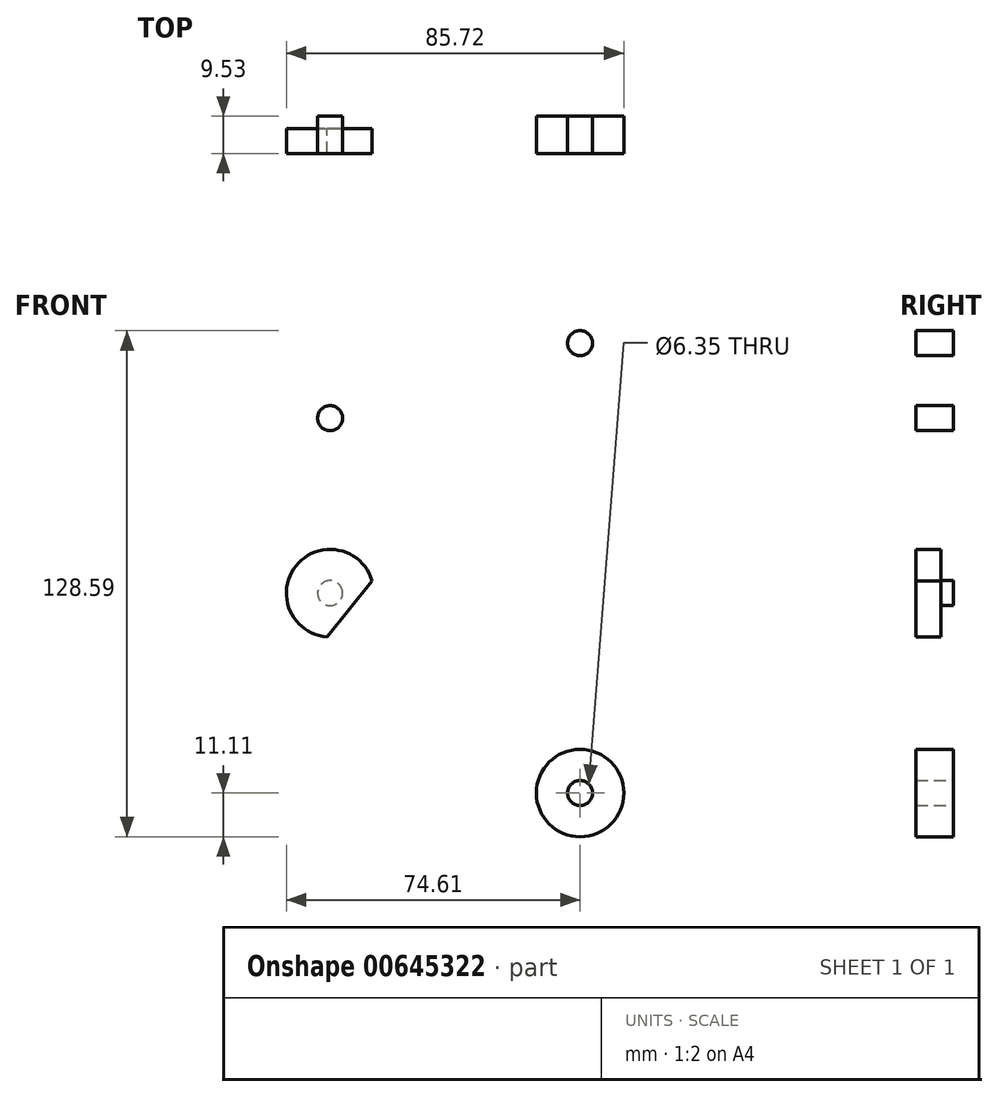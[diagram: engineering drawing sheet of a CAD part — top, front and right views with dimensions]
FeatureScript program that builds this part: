
annotation { "Feature Type Name" : "Feature", "Feature Type Description" : "" }
export const myFeature = defineFeature(function(context is Context, id is Id, definition is map)
    precondition{}
    {
        {
            var Q0;
            Q0=qCreatedBy(makeId("Front.planeOp"),FACE);
            var sketch = newSketch(context, id + "F0", { "sketchPlane" : qUnion([Q0])});
            skLineSegment(sketch, "E0", {"start": v(0, 0) * mm, "end": v(0, 63.5) * mm, "construction": true});
            skLineSegment(sketch, "E1", {"start": v(0, 0) * mm, "end": v(0, -50.8) * mm, "construction": true});
            skCircle(sketch, "E2", {"center": v(0, 0) * mm, "radius": 3.98 * mm});
            skCircle(sketch, "E3", {"center": v(0, 0) * mm, "radius": 15.88 * mm});
            skCircle(sketch, "E4", {"center": v(0, 63.5) * mm, "radius": 3.18 * mm});
            skCircle(sketch, "E5", {"center": v(0, -50.8) * mm, "radius": 3.18 * mm});
            skLineSegment(sketch, "E6", {"start": v(0, 63.5) * mm, "end": v(-44.45, 63.5) * mm, "construction": true});
            skCircle(sketch, "E7", {"center": v(0, 63.5) * mm, "radius": 11.11 * mm});
            skCircle(sketch, "E8", {"center": v(0, -50.8) * mm, "radius": 11.11 * mm});
            skCircle(sketch, "E9", {"center": v(-44.45, 63.5) * mm, "radius": 3.18 * mm});
            skCircle(sketch, "E10", {"center": v(-44.45, 63.5) * mm, "radius": 7.94 * mm});
            skLineSegment(sketch, "E11", {"start": v(0, 0) * mm, "end": v(-63.5, 0) * mm, "construction": true});
            skCircle(sketch, "E12", {"center": v(-63.5, 0) * mm, "radius": 3.18 * mm});
            skCircle(sketch, "E13", {"center": v(-63.5, 0) * mm, "radius": 11.11 * mm});
            skLineSegment(sketch, "E14", {"start": v(-63.5, 0) * mm, "end": v(-63.5, 44.45) * mm, "construction": true});
            skCircle(sketch, "E15", {"center": v(-63.5, 44.45) * mm, "radius": 3.18 * mm});
            skCircle(sketch, "E16", {"center": v(-63.5, 44.45) * mm, "radius": 7.94 * mm});
            skCircle(sketch, "E17", {"center": v(-42.85, 0) * mm, "radius": 3.18 * mm});
            skLineSegment(sketch, "E18", {"start": v(-0.8, 74.58) * mm, "end": v(-45.02, 71.42) * mm});
            skLineSegment(sketch, "E19", {"start": v(11.08, 64.33) * mm, "end": v(15.83, 1.2) * mm});
            skLineSegment(sketch, "E20", {"start": v(11.06, -51.84) * mm, "end": v(15.8, -1.49) * mm});
            skCircle(sketch, "E21", {"center": v(3.18, -36.39) * mm, "radius": 3.18 * mm});
            skLineSegment(sketch, "E22", {"start": v(3.18, -36.39) * mm, "end": v(0, -36.39) * mm, "construction": true});
            skLineSegment(sketch, "E23", {"start": v(-11.06, -51.84) * mm, "end": v(-15.95, 0) * mm});
            skLineSegment(sketch, "E24", {"start": v(-1.2, -15.83) * mm, "end": v(-64.33, -11.08) * mm});
            skLineSegment(sketch, "E25", {"start": v(-74.58, 0.8) * mm, "end": v(-71.42, 45.02) * mm});
            skLineSegment(sketch, "E26", {"start": v(-45.02, 55.58) * mm, "end": v(-19.88, 53.78) * mm});
            skLineSegment(sketch, "E27", {"start": v(-15.83, 1.2) * mm, "end": v(-12.52, 45.26) * mm});
            skArc(sketch, "E28.filletArc", {"start": v(-12.52, 45.26) * mm, "mid": v(-14.43, 51.05) * mm, "end": v(-19.88, 53.78) * mm});
            skLineSegment(sketch, "E29", {"start": v(-45.26, 12.52) * mm, "end": v(-1.2, 15.83) * mm});
            skLineSegment(sketch, "E30", {"start": v(-53.78, 19.88) * mm, "end": v(-55.58, 45.02) * mm});
            skArc(sketch, "E31.filletArc", {"start": v(-53.78, 19.88) * mm, "mid": v(-51.05, 14.43) * mm, "end": v(-45.26, 12.52) * mm});
            skCircle(sketch, "E32", {"center": v(0, 0) * mm, "radius": 3.18 * mm});
            skSolve(sketch);
        }
        {
            var Q0;
            {var subQ0=sQuery(id+"F0.wireOp",EDGE,"E18");Q0=makeQuery(id+"F0.imprint","IMPRINT",FACE,{"disambiguationData":[TD([[makeQuery(id+"F0.imprint","IMPRINT",EDGE,{"derivedFrom":subQ0}),1.0]])]});}
            var Q1;
            Q1=makeQuery(id+"F0.imprint","IMPRINT",FACE,{"disambiguationData":[TD([[makeQuery(id+"F0.imprint","IMPRINT",EDGE,{"derivedFrom":sQuery(id+"F0.wireOp",EDGE,"E9")}),-1.0]])]});
            var Q2;
            Q2=makeQuery(id+"F0.imprint","IMPRINT",FACE,{"disambiguationData":[TD([[makeQuery(id+"F0.imprint","IMPRINT",EDGE,{"derivedFrom":sQuery(id+"F0.wireOp",EDGE,"E4")}),-1.0]])]});
            var Q3;
            {var subQ0=sQuery(id+"F0.wireOp",EDGE,"E27");var subQ1=sQuery(id+"F0.wireOp",EDGE,"E3");var subQ2=makeQuery(id+"F0.imprint","INTERSECT",VERTEX,{"derivedFrom":[subQ1,subQ0]});Q3=makeQuery(id+"F0.imprint","IMPRINT",FACE,{"disambiguationData":[TD([[makeQuery(id+"F0.imprint","IMPRINT",EDGE,{"disambiguationData":[TD([[subQ2,1.0]])],"derivedFrom":subQ1}),-1.0]])]});}
            var Q4;
            Q4=makeQuery(id+"F0.imprint","IMPRINT",FACE,{"disambiguationData":[TD([[makeQuery(id+"F0.imprint","IMPRINT",EDGE,{"derivedFrom":sQuery(id+"F0.wireOp",EDGE,"E2")}),-1.0]])]});
            var Q5;
            {var subQ0=sQuery(id+"F0.wireOp",EDGE,"E20");Q5=makeQuery(id+"F0.imprint","IMPRINT",FACE,{"disambiguationData":[TD([[makeQuery(id+"F0.imprint","IMPRINT",EDGE,{"derivedFrom":subQ0}),1.0]])]});}
            var Q6;
            {var subQ0=sQuery(id+"F0.wireOp",EDGE,"E24");var subQ1=sQuery(id+"F0.wireOp",EDGE,"E3");var subQ2=makeQuery(id+"F0.imprint","INTERSECT",VERTEX,{"derivedFrom":[subQ1,subQ0]});Q6=makeQuery(id+"F0.imprint","IMPRINT",FACE,{"disambiguationData":[TD([[makeQuery(id+"F0.imprint","IMPRINT",EDGE,{"disambiguationData":[TD([[subQ2,1.0]])],"derivedFrom":subQ1}),-1.0]])]});}
            var Q7;
            Q7=makeQuery(id+"F0.imprint","IMPRINT",FACE,{"disambiguationData":[TD([[makeQuery(id+"F0.imprint","IMPRINT",EDGE,{"derivedFrom":sQuery(id+"F0.wireOp",EDGE,"E5")}),-1.0]])]});
            var Q8;
            Q8=makeQuery(id+"F0.imprint","IMPRINT",FACE,{"disambiguationData":[TD([[makeQuery(id+"F0.imprint","IMPRINT",EDGE,{"derivedFrom":sQuery(id+"F0.wireOp",EDGE,"E2")}),1.0]])]});
            extrude(context, id + "F1", {"entities" : qUnion([Q0, Q1, Q2, Q3, Q4, Q5, Q6, Q7, Q8]), "oppositeDirection" : true, "depth" : 3.17 * mm, "offsetDistance" : 25.4 * mm});
        }
        {
            var Q0;
            Q0=makeQuery(id+"F0.imprint","IMPRINT",FACE,{"disambiguationData":[TD([[makeQuery(id+"F0.imprint","IMPRINT",EDGE,{"derivedFrom":sQuery(id+"F0.wireOp",EDGE,"E17")}),-1.0]])]});
            var Q1;
            Q1=makeQuery(id+"F0.imprint","IMPRINT",FACE,{"disambiguationData":[TD([[makeQuery(id+"F0.imprint","IMPRINT",EDGE,{"derivedFrom":sQuery(id+"F0.wireOp",EDGE,"E15")}),-1.0]])]});
            var Q2;
            Q2=makeQuery(id+"F0.imprint","IMPRINT",FACE,{"disambiguationData":[TD([[makeQuery(id+"F0.imprint","IMPRINT",EDGE,{"derivedFrom":sQuery(id+"F0.wireOp",EDGE,"E12")}),-1.0]])]});
            var Q3;
            {var subQ0=sQuery(id+"F0.wireOp",EDGE,"E27");var subQ1=sQuery(id+"F0.wireOp",EDGE,"E3");var subQ2=makeQuery(id+"F0.imprint","INTERSECT",VERTEX,{"derivedFrom":[subQ1,subQ0]});Q3=makeQuery(id+"F0.imprint","IMPRINT",FACE,{"disambiguationData":[TD([[makeQuery(id+"F0.imprint","IMPRINT",EDGE,{"disambiguationData":[TD([[subQ2,1.0]])],"derivedFrom":subQ1}),-1.0]])]});}
            var Q4;
            Q4=makeQuery(id+"F0.imprint","IMPRINT",FACE,{"disambiguationData":[TD([[makeQuery(id+"F0.imprint","IMPRINT",EDGE,{"derivedFrom":sQuery(id+"F0.wireOp",EDGE,"E2")}),-1.0]])]});
            var Q5;
            {var subQ0=sQuery(id+"F0.wireOp",EDGE,"E24");var subQ1=sQuery(id+"F0.wireOp",EDGE,"E3");var subQ2=makeQuery(id+"F0.imprint","INTERSECT",VERTEX,{"derivedFrom":[subQ1,subQ0]});Q5=makeQuery(id+"F0.imprint","IMPRINT",FACE,{"disambiguationData":[TD([[makeQuery(id+"F0.imprint","IMPRINT",EDGE,{"disambiguationData":[TD([[subQ2,1.0]])],"derivedFrom":subQ1}),-1.0]])]});}
            var Q6;
            Q6=makeQuery(id+"F0.imprint","IMPRINT",FACE,{"disambiguationData":[TD([[makeQuery(id+"F0.imprint","IMPRINT",EDGE,{"derivedFrom":sQuery(id+"F0.wireOp",EDGE,"E2")}),1.0]])]});
            extrude(context, id + "F2", {"entities" : qUnion([Q0, Q1, Q2, Q3, Q4, Q5, Q6]), "depth" : 3.17 * mm, "offsetDistance" : 25.4 * mm});
        }
        {
            var Q0;
            Q0=makeQuery(id+"F1.opExtrude","CAP_FACE",FACE,{"disambiguationData":[OSD([sQuery(id+"F0.wireOp",EDGE,"E3"),sQuery(id+"F0.wireOp",EDGE,"E4"),sQuery(id+"F0.wireOp",EDGE,"E5"),sQuery(id+"F0.wireOp",EDGE,"E7"),sQuery(id+"F0.wireOp",EDGE,"E8"),sQuery(id+"F0.wireOp",EDGE,"E9"),sQuery(id+"F0.wireOp",EDGE,"E10"),sQuery(id+"F0.wireOp",EDGE,"E18"),sQuery(id+"F0.wireOp",EDGE,"E19"),sQuery(id+"F0.wireOp",EDGE,"E20"),sQuery(id+"F0.wireOp",EDGE,"E21"),sQuery(id+"F0.wireOp",EDGE,"E23"),sQuery(id+"F0.wireOp",EDGE,"E26"),sQuery(id+"F0.wireOp",EDGE,"E27"),sQuery(id+"F0.wireOp",EDGE,"E28.filletArc"),sQuery(id+"F0.wireOp",EDGE,"E32")])],"isStart":false});
            var sketch = newSketch(context, id + "F3", { "sketchPlane" : qUnion([Q0])});
            skCircle(sketch, "E33", {"center": v(0, 0) * mm, "radius": 3.98 * mm});
            skCircle(sketch, "E34", {"center": v(0, -50.8) * mm, "radius": 11.11 * mm});
            skSolve(sketch);
        }
        {
            var Q0;
            Q0=makeQuery(id+"F0.imprint","IMPRINT",FACE,{"disambiguationData":[TD([[makeQuery(id+"F0.imprint","IMPRINT",EDGE,{"derivedFrom":sQuery(id+"F0.wireOp",EDGE,"E12")}),-1.0]])]});
            var sketch = newSketch(context, id + "F4", { "sketchPlane" : qUnion([Q0])});
            skCircle(sketch, "E35", {"center": v(-63.5, 0) * mm, "radius": 11.11 * mm});
            skSolve(sketch);
        }
        {
            var Q0;
            Q0=qCreatedBy(makeId("Front.planeOp"),FACE);
            cPlane(context, id + "F5", {"entities" : qUnion([Q0]), "cplaneType" : CPlaneType.OFFSET, "offset" : 9.52 * mm, "width" : 152.4 * mm, "height" : 152.4 * mm});
        }
        {
            var Q0;
            Q0=makeQuery(id+"F0.imprint","IMPRINT",FACE,{"disambiguationData":[TD([[makeQuery(id+"F0.imprint","IMPRINT",EDGE,{"derivedFrom":sQuery(id+"F0.wireOp",EDGE,"E17")}),-1.0]])]});
            var sketch = newSketch(context, id + "F6", { "sketchPlane" : qUnion([Q0])});
            skLineSegment(sketch, "E36", {"start": v(-52.84, 3.15) * mm, "end": v(-64.24, -11.09) * mm});
            skLineSegment(sketch, "E37", {"start": v(0, -50.8) * mm, "end": v(-58.54, -3.97) * mm, "construction": true});
            skCircle(sketch, "E38.0", {"center": v(-63.5, 0) * mm, "radius": 11.11 * mm});
            skSolve(sketch);
        }
        {
            var Q0;
            {var subQ0=sQuery(id+"F6.wireOp",EDGE,"E36");Q0=makeQuery(id+"F6.imprint","IMPRINT",FACE,{"disambiguationData":[TD([[makeQuery(id+"F6.imprint","IMPRINT",EDGE,{"derivedFrom":subQ0}),-1.0]])]});}
            var Q1;
            Q1=makeQuery(id+"F0.imprint","IMPRINT",FACE,{"disambiguationData":[TD([[makeQuery(id+"F0.imprint","IMPRINT",EDGE,{"derivedFrom":sQuery(id+"F0.wireOp",EDGE,"E5")}),-1.0]])]});
            var Q2;
            Q2=makeQuery(id+"F0.imprint","IMPRINT",FACE,{"disambiguationData":[TD([[makeQuery(id+"F0.imprint","IMPRINT",EDGE,{"derivedFrom":sQuery(id+"F0.wireOp",EDGE,"E4")}),1.0]])]});
            var Q3;
            Q3=makeQuery(id+"F0.imprint","IMPRINT",FACE,{"disambiguationData":[TD([[makeQuery(id+"F0.imprint","IMPRINT",EDGE,{"derivedFrom":sQuery(id+"F0.wireOp",EDGE,"E15")}),1.0]])]});
            var Q4;
            Q4=qCreatedBy(id+"F5.planeOp",FACE);
            extrude(context, id + "F7", {"entities" : qUnion([Q0, Q1, Q2, Q3]), "endBound" : BoundingType.UP_TO_SURFACE, "depth" : 25.4 * mm, "endBoundEntityFace" : qUnion([Q4]), "offsetDistance" : 25.4 * mm});
        }
        {
            var Q0;
            Q0=makeQuery(id+"F2.opExtrude","SWEPT_BODY",BODY,{"disambiguationData":[OSD([sQuery(id+"F0.wireOp",EDGE,"E3"),sQuery(id+"F0.wireOp",EDGE,"E12"),sQuery(id+"F0.wireOp",EDGE,"E13"),sQuery(id+"F0.wireOp",EDGE,"E15"),sQuery(id+"F0.wireOp",EDGE,"E16"),sQuery(id+"F0.wireOp",EDGE,"E17"),sQuery(id+"F0.wireOp",EDGE,"E24"),sQuery(id+"F0.wireOp",EDGE,"E25"),sQuery(id+"F0.wireOp",EDGE,"E29"),sQuery(id+"F0.wireOp",EDGE,"E30"),sQuery(id+"F0.wireOp",EDGE,"E31.filletArc"),sQuery(id+"F0.wireOp",EDGE,"E32")])]});
            var Q1;
            Q1=makeQuery(id+"F1.opExtrude","SWEPT_BODY",BODY,{"disambiguationData":[OSD([sQuery(id+"F0.wireOp",EDGE,"E3"),sQuery(id+"F0.wireOp",EDGE,"E4"),sQuery(id+"F0.wireOp",EDGE,"E5"),sQuery(id+"F0.wireOp",EDGE,"E7"),sQuery(id+"F0.wireOp",EDGE,"E8"),sQuery(id+"F0.wireOp",EDGE,"E9"),sQuery(id+"F0.wireOp",EDGE,"E10"),sQuery(id+"F0.wireOp",EDGE,"E18"),sQuery(id+"F0.wireOp",EDGE,"E19"),sQuery(id+"F0.wireOp",EDGE,"E20"),sQuery(id+"F0.wireOp",EDGE,"E21"),sQuery(id+"F0.wireOp",EDGE,"E23"),sQuery(id+"F0.wireOp",EDGE,"E26"),sQuery(id+"F0.wireOp",EDGE,"E27"),sQuery(id+"F0.wireOp",EDGE,"E28.filletArc"),sQuery(id+"F0.wireOp",EDGE,"E32")])]});
            var Q2;
            Q2=makeQuery(id+"F7.opExtrude","SWEPT_BODY",BODY,{"disambiguationData":[OSD([sQuery(id+"F6.wireOp",EDGE,"E36"),sQuery(id+"F6.wireOp",EDGE,"E38.0")])]});
            var Q3;
            Q3=makeQuery(id+"F7.opExtrude","SWEPT_BODY",BODY,{"disambiguationData":[OSD([sQuery(id+"F0.wireOp",EDGE,"E15")])]});
            var Q4;
            Q4=makeQuery(id+"F7.opExtrude","SWEPT_BODY",BODY,{"disambiguationData":[OSD([sQuery(id+"F0.wireOp",EDGE,"E4")])]});
            var Q5;
            Q5=makeQuery(id+"F7.opExtrude","SWEPT_BODY",BODY,{"disambiguationData":[OSD([sQuery(id+"F0.wireOp",EDGE,"E5"),sQuery(id+"F0.wireOp",EDGE,"E8")])]});
            booleanBodies(context, id + "F8", {"operationType" : BooleanOperationType.SUBTRACTION, "tools" : qUnion([Q0, Q1]), "targets" : qUnion([Q2, Q3, Q4, Q5])});
        }
    });
